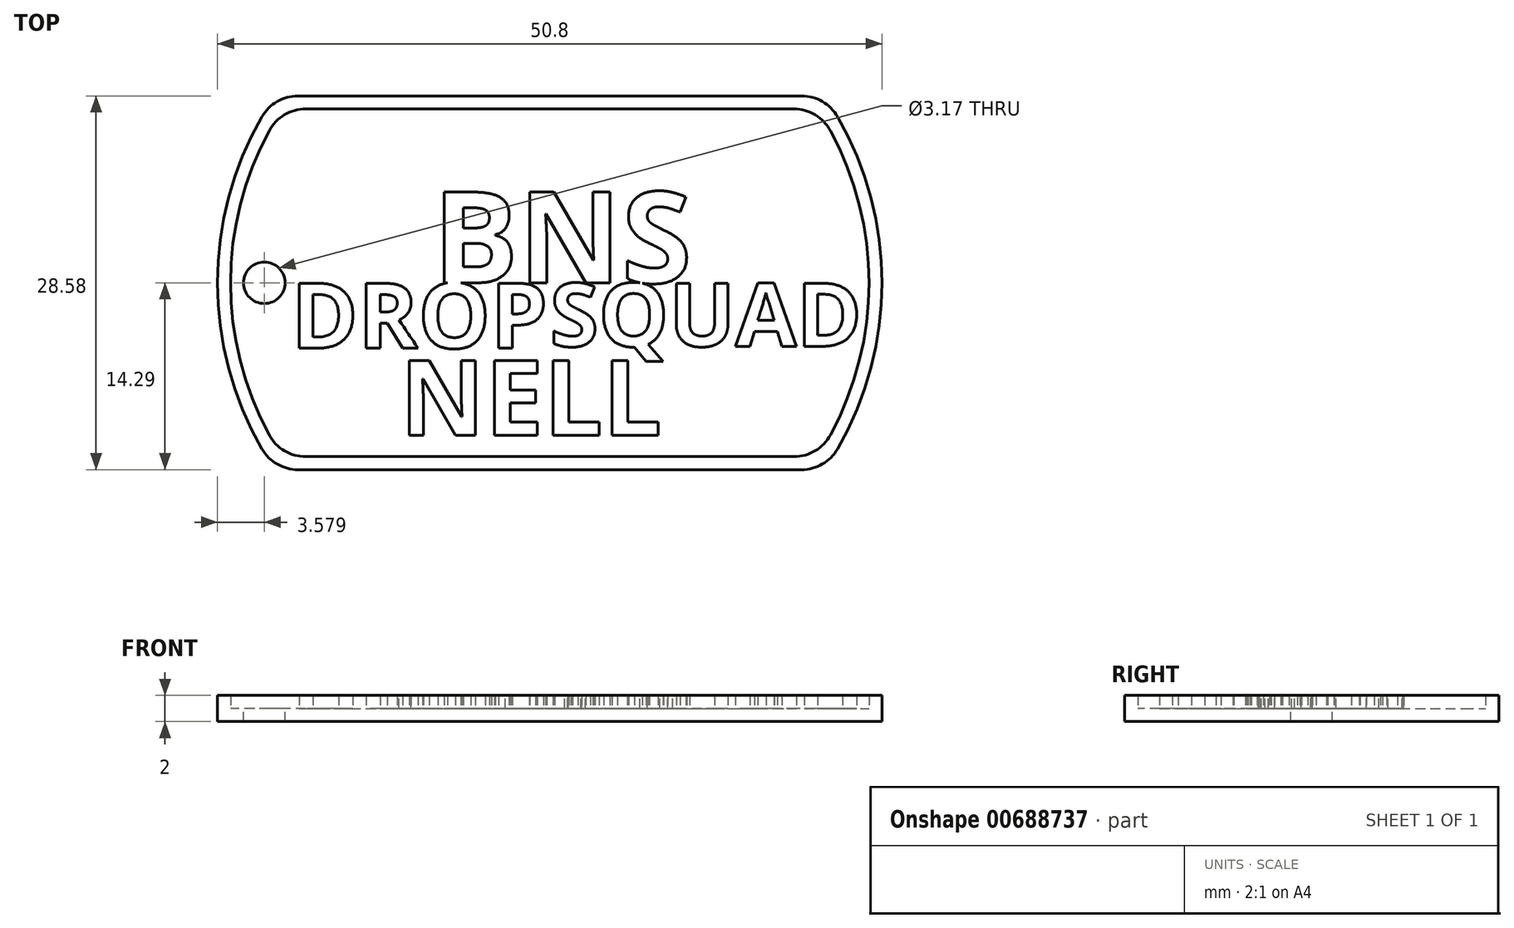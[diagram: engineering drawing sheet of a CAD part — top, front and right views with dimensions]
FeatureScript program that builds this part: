
annotation { "Feature Type Name" : "Feature", "Feature Type Description" : "" }
export const myFeature = defineFeature(function(context is Context, id is Id, definition is map)
    precondition{}
    {
        {
            var Q0;
            Q0=qCreatedBy(makeId("Top.planeOp"),FACE);
            var sketch = newSketch(context, id + "F0", { "sketchPlane" : qUnion([Q0])});
            skArc(sketch, "E0", {"start": v(-22, 12.7) * mm, "mid": v(-25.4, 0) * mm, "end": v(-22, -12.7) * mm});
            skLineSegment(sketch, "E1.top", {"start": v(-19.25, -14.29) * mm, "end": v(19.25, -14.29) * mm});
            skArc(sketch, "E2.trimOffspring", {"start": v(22, -12.7) * mm, "mid": v(25.4, 0) * mm, "end": v(22, 12.7) * mm});
            skLineSegment(sketch, "E3", {"start": v(-19.25, 14.29) * mm, "end": v(19.25, 14.29) * mm});
            skPoint(sketch, "E4.visualSharp", {"position": v(-21, 14.29) * mm});
            skArc(sketch, "E4.filletArc", {"start": v(-19.25, 14.29) * mm, "mid": v(-20.83, 13.86) * mm, "end": v(-22, 12.7) * mm});
            skPoint(sketch, "E5.visualSharp", {"position": v(21, 14.29) * mm});
            skArc(sketch, "E5.filletArc", {"start": v(22, 12.7) * mm, "mid": v(20.83, 13.86) * mm, "end": v(19.25, 14.29) * mm});
            skPoint(sketch, "E6.visualSharp", {"position": v(21, -14.29) * mm});
            skArc(sketch, "E6.filletArc", {"start": v(19.25, -14.29) * mm, "mid": v(20.83, -13.86) * mm, "end": v(22, -12.7) * mm});
            skPoint(sketch, "E7.visualSharp", {"position": v(-21, -14.29) * mm});
            skArc(sketch, "E7.filletArc", {"start": v(-22, -12.7) * mm, "mid": v(-20.83, -13.86) * mm, "end": v(-19.25, -14.29) * mm});
            skSolve(sketch);
        }
        {
            var Q0;
            Q0=makeQuery(id+"F0.imprint","IMPRINT",FACE,{"disambiguationData":[TD([[makeQuery(id+"F0.imprint","IMPRINT",EDGE,{"derivedFrom":sQuery(id+"F0.wireOp",EDGE,"E0")}),1.0]])]});
            extrude(context, id + "F1", {"entities" : qUnion([Q0]), "depth" : 1 * mm, "offsetDistance" : 25.4 * mm});
        }
        {
            var Q0;
            Q0=makeQuery(id+"F1.opExtrude","CAP_FACE",FACE,{"disambiguationData":[OSD([sQuery(id+"F0.wireOp",EDGE,"E0"),sQuery(id+"F0.wireOp",EDGE,"E1.top"),sQuery(id+"F0.wireOp",EDGE,"E2.trimOffspring"),sQuery(id+"F0.wireOp",EDGE,"E3"),sQuery(id+"F0.wireOp",EDGE,"E4.filletArc"),sQuery(id+"F0.wireOp",EDGE,"E5.filletArc"),sQuery(id+"F0.wireOp",EDGE,"E6.filletArc"),sQuery(id+"F0.wireOp",EDGE,"E7.filletArc")])],"isStart":false});
            var sketch = newSketch(context, id + "F2", { "sketchPlane" : qUnion([Q0])});
            skLineSegment(sketch, "E8.0", {"start": v(-18.66, 13.29) * mm, "end": v(18.66, 13.29) * mm});
            skArc(sketch, "E8.1", {"start": v(-21.45, 11.63) * mm, "mid": v(-24.4, 0) * mm, "end": v(-21.45, -11.63) * mm});
            skLineSegment(sketch, "E8.2", {"start": v(-18.66, -13.29) * mm, "end": v(18.66, -13.29) * mm});
            skArc(sketch, "E8.3", {"start": v(21.45, -11.63) * mm, "mid": v(24.4, 0) * mm, "end": v(21.45, 11.63) * mm});
            skPoint(sketch, "E9.visualSharp", {"position": v(-20.46, 13.29) * mm});
            skArc(sketch, "E9.filletArc", {"start": v(-18.66, 13.29) * mm, "mid": v(-20.29, 12.84) * mm, "end": v(-21.45, 11.63) * mm});
            skPoint(sketch, "E10.visualSharp", {"position": v(20.46, 13.29) * mm});
            skArc(sketch, "E10.filletArc", {"start": v(21.45, 11.63) * mm, "mid": v(20.29, 12.84) * mm, "end": v(18.66, 13.29) * mm});
            skPoint(sketch, "E11.visualSharp", {"position": v(20.46, -13.29) * mm});
            skArc(sketch, "E11.filletArc", {"start": v(18.66, -13.29) * mm, "mid": v(20.29, -12.84) * mm, "end": v(21.45, -11.63) * mm});
            skPoint(sketch, "E12.visualSharp", {"position": v(-20.46, -13.29) * mm});
            skArc(sketch, "E12.filletArc", {"start": v(-21.45, -11.63) * mm, "mid": v(-20.29, -12.84) * mm, "end": v(-18.66, -13.29) * mm});
            skLineSegment(sketch, "E13.0", {"start": v(-19.25, 14.29) * mm, "end": v(19.25, 14.29) * mm});
            skArc(sketch, "E13.1", {"start": v(-22, 12.7) * mm, "mid": v(-25.4, 0) * mm, "end": v(-22, -12.7) * mm});
            skLineSegment(sketch, "E13.2", {"start": v(-19.25, -14.29) * mm, "end": v(19.25, -14.29) * mm});
            skArc(sketch, "E13.3", {"start": v(22, -12.7) * mm, "mid": v(25.4, 0) * mm, "end": v(22, 12.7) * mm});
            skPoint(sketch, "E14.visualSharp", {"position": v(-21, -14.29) * mm});
            skArc(sketch, "E14.filletArc", {"start": v(-22, -12.7) * mm, "mid": v(-20.83, -13.86) * mm, "end": v(-19.25, -14.29) * mm});
            skPoint(sketch, "E15.visualSharp", {"position": v(21, -14.29) * mm});
            skArc(sketch, "E15.filletArc", {"start": v(19.25, -14.29) * mm, "mid": v(20.83, -13.86) * mm, "end": v(22, -12.7) * mm});
            skPoint(sketch, "E16.visualSharp", {"position": v(21, 14.29) * mm});
            skArc(sketch, "E16.filletArc", {"start": v(22, 12.7) * mm, "mid": v(20.83, 13.86) * mm, "end": v(19.25, 14.29) * mm});
            skPoint(sketch, "E17.visualSharp", {"position": v(-21, 14.29) * mm});
            skArc(sketch, "E17.filletArc", {"start": v(-19.25, 14.29) * mm, "mid": v(-20.83, 13.86) * mm, "end": v(-22, 12.7) * mm});
            skSolve(sketch);
        }
        {
            var Q0;
            Q0=makeQuery(id+"F2.imprint","IMPRINT",FACE,{"disambiguationData":[TD([[makeQuery(id+"F2.imprint","IMPRINT",EDGE,{"derivedFrom":sQuery(id+"F2.wireOp",EDGE,"E8.0")}),1.0]])]});
            extrude(context, id + "F3", {"entities" : qUnion([Q0]), "operationType" : NewBodyOperationType.ADD, "depth" : 1 * mm, "offsetDistance" : 25.4 * mm});
        }
        {
            var Q0;
            Q0=makeQuery(id+"F1.opExtrude","CAP_FACE",FACE,{"disambiguationData":[OSD([sQuery(id+"F0.wireOp",EDGE,"E0"),sQuery(id+"F0.wireOp",EDGE,"E1.top"),sQuery(id+"F0.wireOp",EDGE,"E2.trimOffspring"),sQuery(id+"F0.wireOp",EDGE,"E3"),sQuery(id+"F0.wireOp",EDGE,"E4.filletArc"),sQuery(id+"F0.wireOp",EDGE,"E5.filletArc"),sQuery(id+"F0.wireOp",EDGE,"E6.filletArc"),sQuery(id+"F0.wireOp",EDGE,"E7.filletArc")])],"isStart":false});
            var sketch = newSketch(context, id + "F4", { "sketchPlane" : qUnion([Q0])});
            skCircle(sketch, "E18", {"center": v(-21.82, 0) * mm, "radius": 1.59 * mm});
            skSolve(sketch);
        }
        {
            var Q0;
            Q0=makeQuery(id+"F4.imprint","IMPRINT",FACE,{"disambiguationData":[TD([[makeQuery(id+"F4.imprint","IMPRINT",EDGE,{"derivedFrom":sQuery(id+"F4.wireOp",EDGE,"E18")}),1.0]])]});
            extrude(context, id + "F5", {"entities" : qUnion([Q0]), "operationType" : NewBodyOperationType.REMOVE, "oppositeDirection" : true, "depth" : 1 * mm, "offsetDistance" : 25.4 * mm});
        }
        {
            var Q0;
            Q0=makeQuery(id+"F1.opExtrude","CAP_FACE",FACE,{"disambiguationData":[OSD([sQuery(id+"F0.wireOp",EDGE,"E0"),sQuery(id+"F0.wireOp",EDGE,"E1.top"),sQuery(id+"F0.wireOp",EDGE,"E2.trimOffspring"),sQuery(id+"F0.wireOp",EDGE,"E3"),sQuery(id+"F0.wireOp",EDGE,"E4.filletArc"),sQuery(id+"F0.wireOp",EDGE,"E5.filletArc"),sQuery(id+"F0.wireOp",EDGE,"E6.filletArc"),sQuery(id+"F0.wireOp",EDGE,"E7.filletArc")])],"isStart":false});
            var sketch = newSketch(context, id + "F6", { "sketchPlane" : qUnion([Q0])});
            skText(sketch, "E19", { "text": "BNS", "fontName": "OpenSans-Bold.ttf"});
            skText(sketch, "E20", { "text": "DROP", "fontName": "OpenSans-Bold.ttf"});
            skText(sketch, "E21", { "text": "SQUAD", "fontName": "OpenSans-Bold.ttf"});
            skText(sketch, "E22", { "text": "NELL", "fontName": "OpenSans-Bold.ttf"});
            const initialGuessF6  = {"E19": [-0.00895, 0, 1, 0, 0.007], "E20": [-0.01979, -0.005, 1, 0, 0.005], "E21": [0, -0.00486, 1, 0, 0.00486], "E22": [-0.01146, -0.01165, 1, 0, 0.00576]};
            skSetInitialGuess(sketch, initialGuessF6);
            skSolve(sketch);
        }
        {
            var Q0;
            Q0 = qSketchRegion(id + "F6", true);
            extrude(context, id + "F7", {"entities" : qUnion([Q0]), "operationType" : NewBodyOperationType.ADD, "depth" : 1 * mm, "offsetDistance" : 25.4 * mm});
        }
    });
